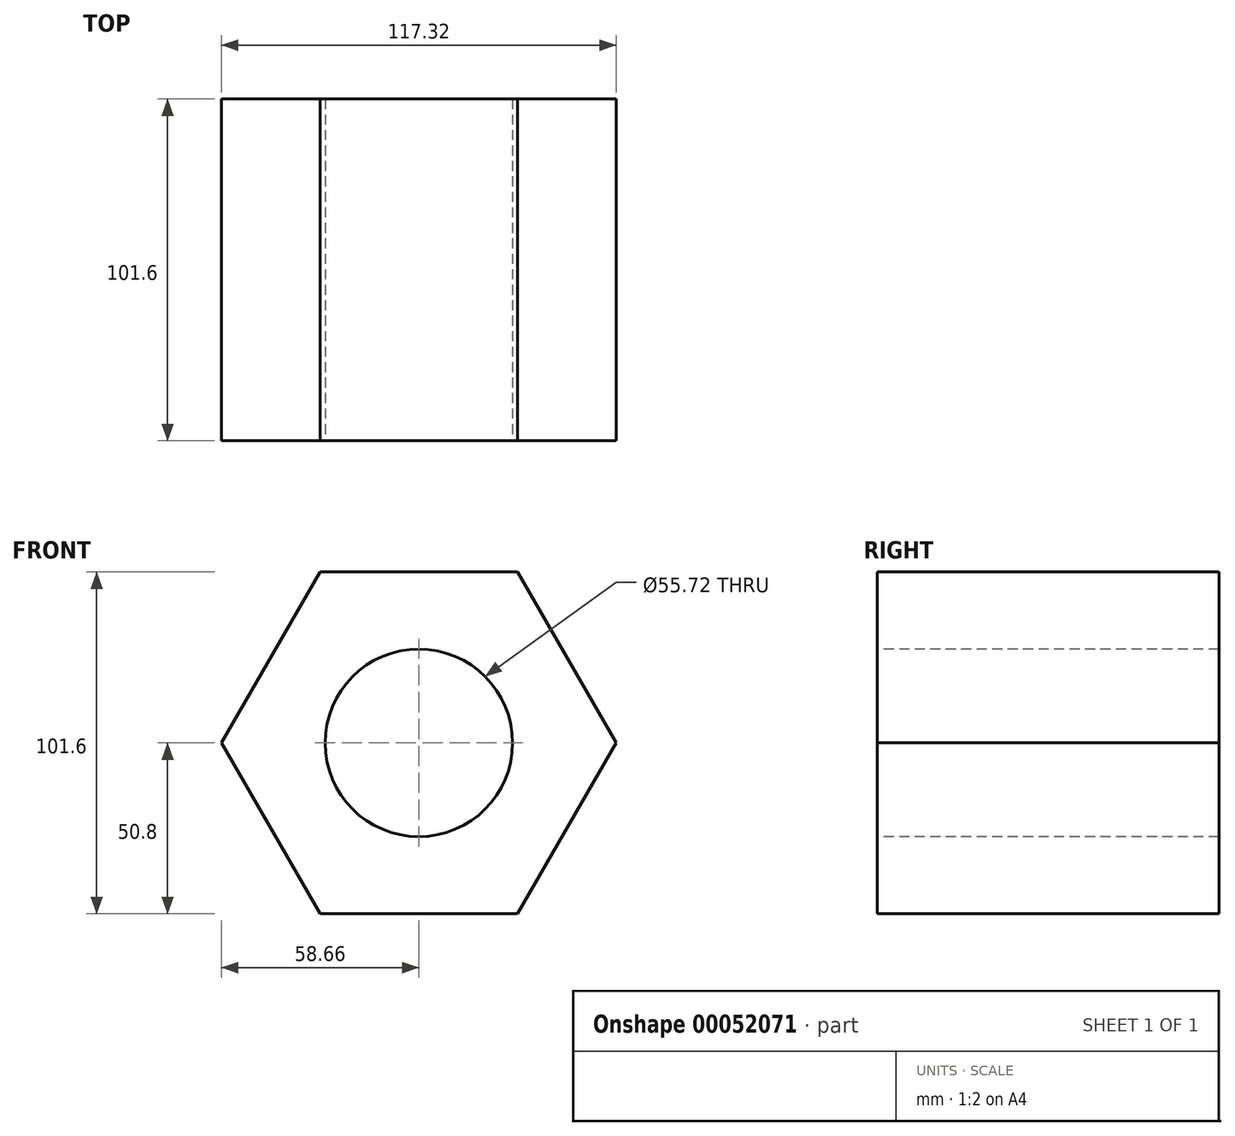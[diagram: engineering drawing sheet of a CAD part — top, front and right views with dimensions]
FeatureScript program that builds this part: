
annotation { "Feature Type Name" : "Feature", "Feature Type Description" : "" }
export const myFeature = defineFeature(function(context is Context, id is Id, definition is map)
    precondition{}
    {
        {
            var Q0;
            Q0=qCreatedBy(makeId("Front.planeOp"),FACE);
            var sketch = newSketch(context, id + "F0", { "sketchPlane" : qUnion([Q0])});
            skCircle(sketch, "E0.cCircle", {"center": v(0, 0) * mm, "radius": 50.8 * mm, "construction": true});
            skLineSegment(sketch, "E0.0", {"start": v(-29.33, 50.8) * mm, "end": v(29.33, 50.8) * mm});
            skLineSegment(sketch, "E0.1", {"start": v(29.33, 50.8) * mm, "end": v(58.66, 0) * mm});
            skLineSegment(sketch, "E0.2", {"start": v(58.66, 0) * mm, "end": v(29.33, -50.8) * mm});
            skLineSegment(sketch, "E0.3", {"start": v(29.33, -50.8) * mm, "end": v(-29.33, -50.8) * mm});
            skLineSegment(sketch, "E0.4", {"start": v(-29.33, -50.8) * mm, "end": v(-58.66, 0) * mm});
            skLineSegment(sketch, "E0.5", {"start": v(-58.66, 0) * mm, "end": v(-29.33, 50.8) * mm});
            skPoint(sketch, "E0.0.midPoint", {"position": v(0, 50.8) * mm});
            skSolve(sketch);
        }
        {
            var Q0;
            Q0 = qSketchRegion(id + "F0", true);
            extrude(context, id + "F1", {"entities" : qUnion([Q0]), "depth" : 101.6 * mm});
        }
        {
            var Q0;
            Q0=makeQuery(id+"F1.opExtrude","CAP_FACE",FACE,{"disambiguationData":[OSD([sQuery(id+"F0.wireOp",EDGE,"E0.0"),sQuery(id+"F0.wireOp",EDGE,"E0.1"),sQuery(id+"F0.wireOp",EDGE,"E0.2"),sQuery(id+"F0.wireOp",EDGE,"E0.3"),sQuery(id+"F0.wireOp",EDGE,"E0.4"),sQuery(id+"F0.wireOp",EDGE,"E0.5")])],"isStart":false});
            var sketch = newSketch(context, id + "F2", { "sketchPlane" : qUnion([Q0])});
            skCircle(sketch, "E1", {"center": v(0, 0) * mm, "radius": 27.86 * mm});
            skSolve(sketch);
        }
        {
            var Q0;
            Q0 = qSketchRegion(id + "F2", true);
            extrude(context, id + "F3", {"entities" : qUnion([Q0]), "operationType" : NewBodyOperationType.REMOVE, "oppositeDirection" : true, "depth" : 101.6 * mm});
        }
    });
